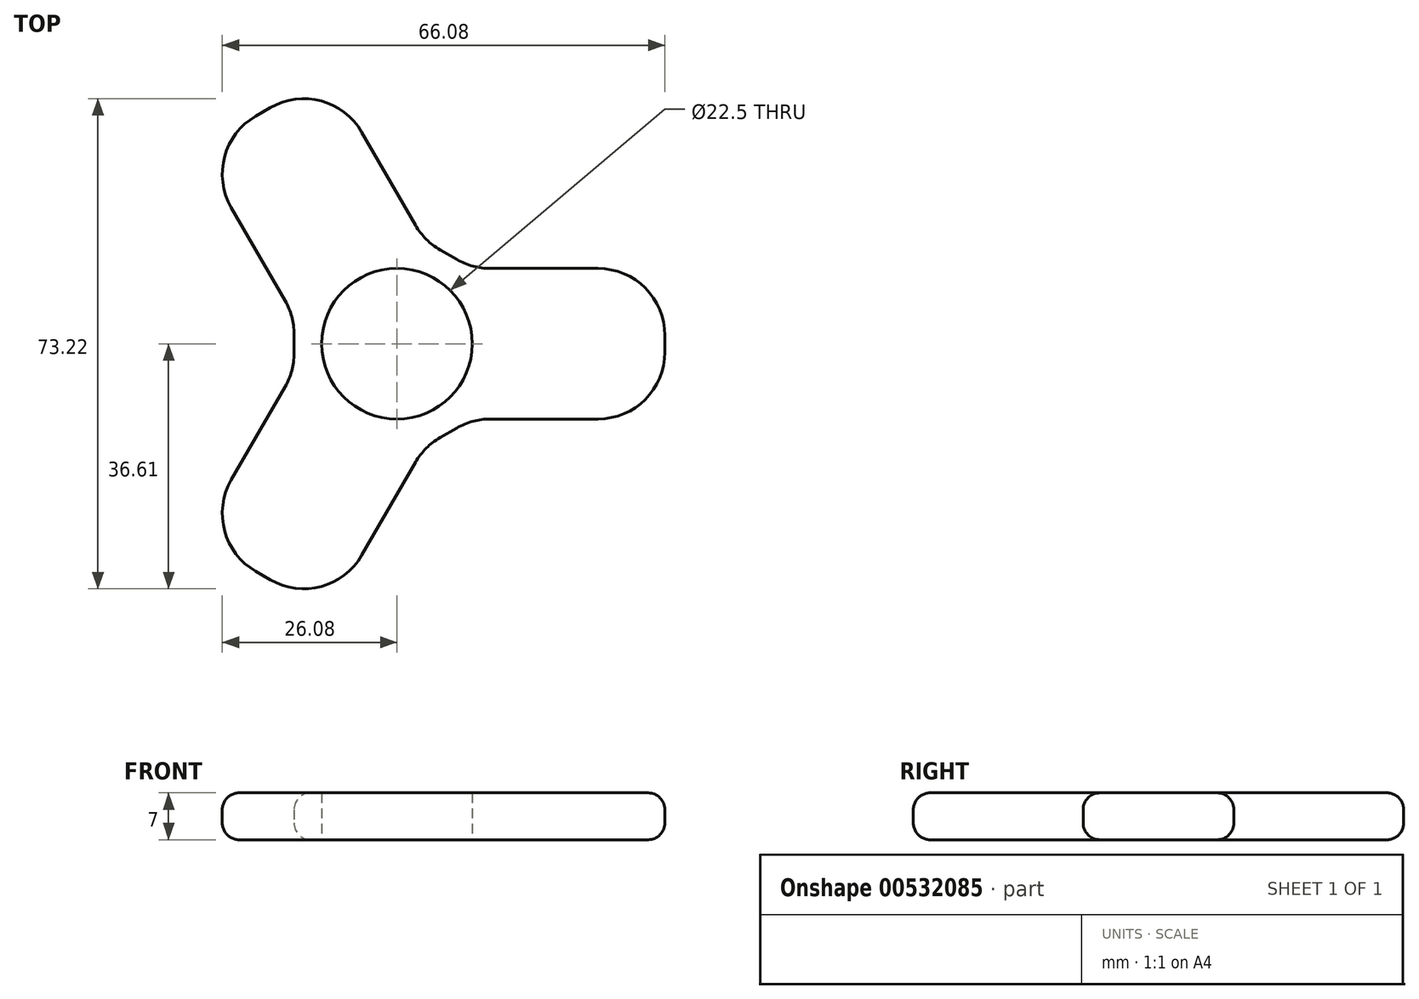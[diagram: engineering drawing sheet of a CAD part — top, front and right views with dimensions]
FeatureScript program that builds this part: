
annotation { "Feature Type Name" : "Feature", "Feature Type Description" : "" }
export const myFeature = defineFeature(function(context is Context, id is Id, definition is map)
    precondition{}
    {
        {
            var Q0;
            Q0=qCreatedBy(makeId("Top.planeOp"),FACE);
            var sketch = newSketch(context, id + "F0", { "sketchPlane" : qUnion([Q0])});
            skCircle(sketch, "E0", {"center": v(0, 0) * mm, "radius": 4 * mm});
            skCircle(sketch, "E1", {"center": v(0, 0) * mm, "radius": 11 * mm});
            skCircle(sketch, "E2", {"center": v(0, 0) * mm, "radius": 11.25 * mm});
            skLineSegment(sketch, "E3.0", {"start": v(13.93, -11.25) * mm, "end": v(30, -11.25) * mm});
            skLineSegment(sketch, "E4.MirrorCS", {"start": v(13.93, 11.25) * mm, "end": v(30, 11.25) * mm});
            skLineSegment(sketch, "E5", {"start": v(40, 1.25) * mm, "end": v(40, -1.25) * mm});
            skPoint(sketch, "E6.visualSharp", {"position": v(40, 11.25) * mm});
            skArc(sketch, "E6.filletArc", {"start": v(40, 1.25) * mm, "mid": v(37.07, 8.32) * mm, "end": v(30, 11.25) * mm});
            skPoint(sketch, "E7.visualSharp", {"position": v(40, -11.25) * mm});
            skArc(sketch, "E7.filletArc", {"start": v(30, -11.25) * mm, "mid": v(37.07, -8.32) * mm, "end": v(40, -1.25) * mm});
            skLineSegment(sketch, "E8.MirrorCS", {"start": v(2.78, 17.69) * mm, "end": v(-5.26, 31.6) * mm});
            skArc(sketch, "E9.MirrorCS", {"start": v(-18.92, 35.27) * mm, "mid": v(-11.33, 36.27) * mm, "end": v(-5.26, 31.6) * mm});
            skLineSegment(sketch, "E10.MirrorCS", {"start": v(-16.7, 6.44) * mm, "end": v(-24.74, 20.36) * mm});
            skArc(sketch, "E11.MirrorCS", {"start": v(-24.74, 20.36) * mm, "mid": v(-25.74, 27.94) * mm, "end": v(-21.08, 34.02) * mm});
            skLineSegment(sketch, "E12.MirrorCS", {"start": v(-16.7, -6.44) * mm, "end": v(-24.74, -20.36) * mm});
            skArc(sketch, "E13.MirrorCS", {"start": v(-21.08, -34.02) * mm, "mid": v(-25.74, -27.94) * mm, "end": v(-24.74, -20.36) * mm});
            skArc(sketch, "E14.MirrorCS", {"start": v(-5.26, -31.6) * mm, "mid": v(-11.33, -36.27) * mm, "end": v(-18.92, -35.27) * mm});
            skLineSegment(sketch, "E15.MirrorCS", {"start": v(2.78, -17.69) * mm, "end": v(-5.26, -31.6) * mm});
            skLineSegment(sketch, "E16", {"start": v(-15.37, 1.44) * mm, "end": v(-15.37, -1.44) * mm});
            skLineSegment(sketch, "E17", {"start": v(6.44, 14.03) * mm, "end": v(8.93, 12.59) * mm});
            skLineSegment(sketch, "E18", {"start": v(6.44, -14.03) * mm, "end": v(8.93, -12.59) * mm});
            skLineSegment(sketch, "E19", {"start": v(-21.08, -34.02) * mm, "end": v(-18.92, -35.27) * mm});
            skLineSegment(sketch, "E20", {"start": v(-21.08, 34.02) * mm, "end": v(-18.92, 35.27) * mm});
            skPoint(sketch, "E21.visualSharp", {"position": v(-15.37, -4.12) * mm});
            skArc(sketch, "E21.filletArc", {"start": v(-16.7, -6.44) * mm, "mid": v(-15.7, -4.03) * mm, "end": v(-15.37, -1.44) * mm});
            skPoint(sketch, "E22.visualSharp", {"position": v(-15.37, 4.12) * mm});
            skArc(sketch, "E22.filletArc", {"start": v(-15.37, 1.44) * mm, "mid": v(-15.7, 4.03) * mm, "end": v(-16.7, 6.44) * mm});
            skPoint(sketch, "E23.visualSharp", {"position": v(4.12, 15.37) * mm});
            skArc(sketch, "E23.filletArc", {"start": v(2.78, 17.69) * mm, "mid": v(4.37, 15.62) * mm, "end": v(6.44, 14.03) * mm});
            skPoint(sketch, "E24.visualSharp", {"position": v(11.25, 11.25) * mm});
            skArc(sketch, "E24.filletArc", {"start": v(8.93, 12.59) * mm, "mid": v(11.34, 11.6) * mm, "end": v(13.93, 11.25) * mm});
            skPoint(sketch, "E25.visualSharp", {"position": v(11.25, -11.25) * mm});
            skArc(sketch, "E25.filletArc", {"start": v(13.93, -11.25) * mm, "mid": v(11.34, -11.6) * mm, "end": v(8.93, -12.59) * mm});
            skPoint(sketch, "E26.visualSharp", {"position": v(4.12, -15.37) * mm});
            skArc(sketch, "E26.filletArc", {"start": v(6.44, -14.03) * mm, "mid": v(4.37, -15.62) * mm, "end": v(2.78, -17.69) * mm});
            skSolve(sketch);
        }
        {
            var Q0;
            Q0=makeQuery(id+"F0.imprint","IMPRINT",FACE,{"disambiguationData":[TD([[makeQuery(id+"F0.imprint","IMPRINT",EDGE,{"derivedFrom":sQuery(id+"F0.wireOp",EDGE,"E2")}),-1.0]])]});
            extrude(context, id + "F1", {"entities" : qUnion([Q0]), "depth" : 7 * mm, "offsetDistance" : 25 * mm});
        }
        {
            var Q0;
            Q0=makeQuery(id+"F1.opExtrude","CAP_EDGE",EDGE,{"disambiguationData":[OSD([sQuery(id+"F0.wireOp",EDGE,"E15.MirrorCS")])],"isStart":false});
            var Q1;
            Q1=makeQuery(id+"F1.opExtrude","CAP_EDGE",EDGE,{"disambiguationData":[OSD([sQuery(id+"F0.wireOp",EDGE,"E4.MirrorCS")])],"isStart":true});
            fillet(context, id + "F2", {"entities" : qUnion([Q0, Q1]), "radius" : 2.5 * mm, "tangentPropagation" : true, "allowEdgeOverflow" : false});
        }
    });
